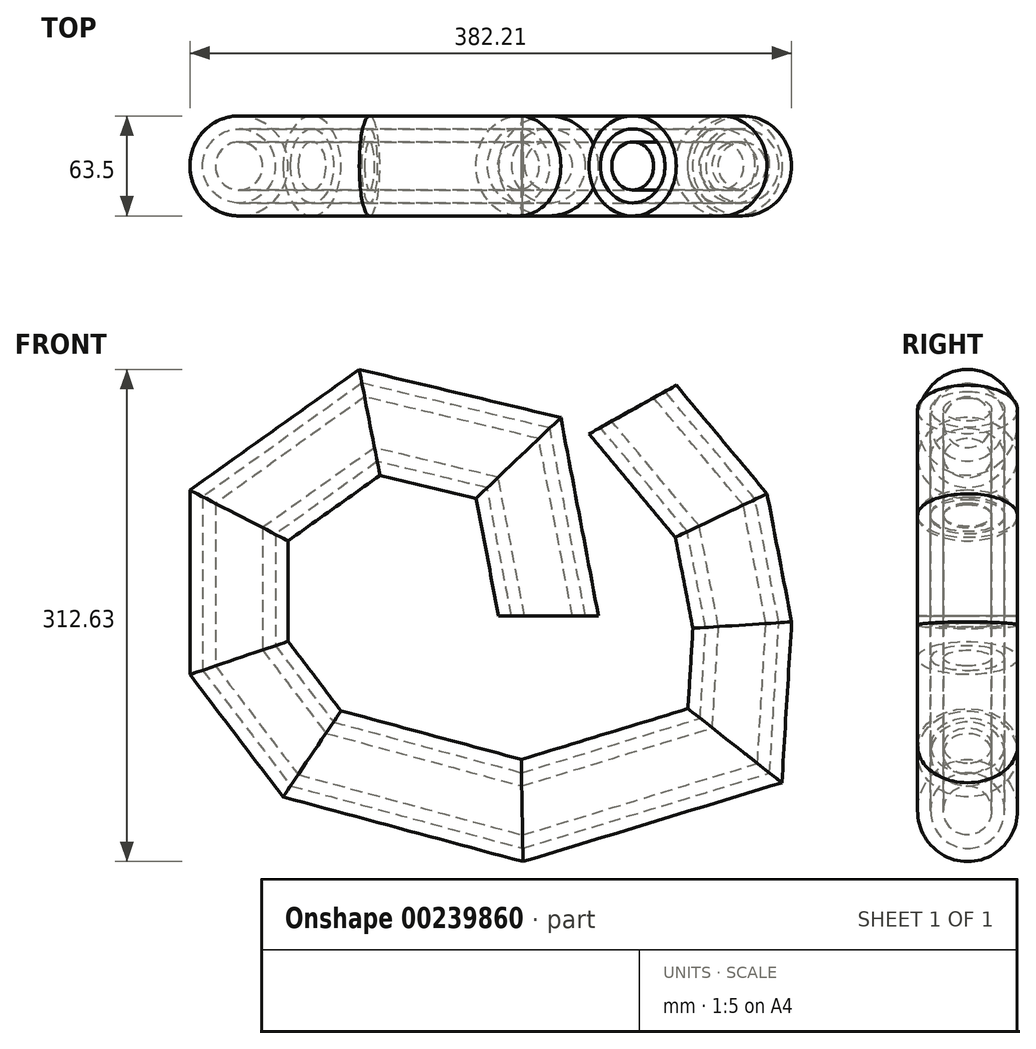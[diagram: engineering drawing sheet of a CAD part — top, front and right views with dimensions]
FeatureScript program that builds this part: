
annotation { "Feature Type Name" : "Feature", "Feature Type Description" : "" }
export const myFeature = defineFeature(function(context is Context, id is Id, definition is map)
    precondition{}
    {
        {
            var Q0;
            Q0=qCreatedBy(makeId("Top.planeOp"),FACE);
            var sketch = newSketch(context, id + "F0", { "sketchPlane" : qUnion([Q0])});
            skCircle(sketch, "E0", {"center": v(0, 0) * mm, "radius": 31.75 * mm});
            skCircle(sketch, "E1", {"center": v(0, 0) * mm, "radius": 23.5 * mm});
            skCircle(sketch, "E2", {"center": v(0, 0) * mm, "radius": 15.24 * mm});
            skSolve(sketch);
        }
        {
            var Q0;
            Q0=qCreatedBy(makeId("Front.planeOp"),FACE);
            var sketch = newSketch(context, id + "F1", { "sketchPlane" : qUnion([Q0])});
            skLineSegment(sketch, "E3", {"start": v(0, 0) * mm, "end": v(-19.08, 100.45) * mm});
            skLineSegment(sketch, "E4", {"start": v(-19.08, 100.45) * mm, "end": v(-113.64, 123.07) * mm});
            skLineSegment(sketch, "E5", {"start": v(-113.64, 123.07) * mm, "end": v(-196.6, 63.9) * mm});
            skLineSegment(sketch, "E6", {"start": v(-196.6, 63.9) * mm, "end": v(-196.6, -26.6) * mm});
            skLineSegment(sketch, "E7", {"start": v(-196.6, -26.6) * mm, "end": v(-150.19, -87.5) * mm});
            skLineSegment(sketch, "E8", {"start": v(-150.19, -87.5) * mm, "end": v(-16.76, -123.48) * mm});
            skLineSegment(sketch, "E9", {"start": v(-16.76, -123.48) * mm, "end": v(118.4, -82.29) * mm});
            skLineSegment(sketch, "E10", {"start": v(118.4, -82.29) * mm, "end": v(123.05, -5.71) * mm});
            skLineSegment(sketch, "E11", {"start": v(123.05, -5.71) * mm, "end": v(109.7, 63.9) * mm});
            skLineSegment(sketch, "E12", {"start": v(109.7, 63.9) * mm, "end": v(53.43, 131.2) * mm});
            skSolve(sketch);
        }
        {
            var Q0;
            Q0=makeQuery(id+"F0.imprint","IMPRINT",FACE,{"disambiguationData":[TD([[makeQuery(id+"F0.imprint","IMPRINT",EDGE,{"derivedFrom":sQuery(id+"F0.wireOp",EDGE,"E0")}),1.0]])]});
            var Q1;
            Q1=makeQuery(id+"F0.imprint","IMPRINT",FACE,{"disambiguationData":[TD([[makeQuery(id+"F0.imprint","IMPRINT",EDGE,{"derivedFrom":sQuery(id+"F0.wireOp",EDGE,"E2")}),1.0]])]});
            var Q2;
            Q2=sQuery(id+"F1.wireOp",EDGE,"E3");
            var Q3;
            Q3=sQuery(id+"F1.wireOp",EDGE,"E4");
            var Q4;
            Q4=sQuery(id+"F1.wireOp",EDGE,"E5");
            var Q5;
            Q5=sQuery(id+"F1.wireOp",EDGE,"E6");
            var Q6;
            Q6=sQuery(id+"F1.wireOp",EDGE,"E7");
            var Q7;
            Q7=sQuery(id+"F1.wireOp",EDGE,"E8");
            var Q8;
            Q8=sQuery(id+"F1.wireOp",EDGE,"E9");
            var Q9;
            Q9=sQuery(id+"F1.wireOp",EDGE,"E10");
            var Q10;
            Q10=sQuery(id+"F1.wireOp",EDGE,"E11");
            var Q11;
            Q11=sQuery(id+"F1.wireOp",EDGE,"E12");
            sweep(context, id + "F2", {"profiles" : qUnion([Q0, Q1]), "path" : qUnion([Q2, Q3, Q4, Q5, Q6, Q7, Q8, Q9, Q10, Q11])});
        }
    });
